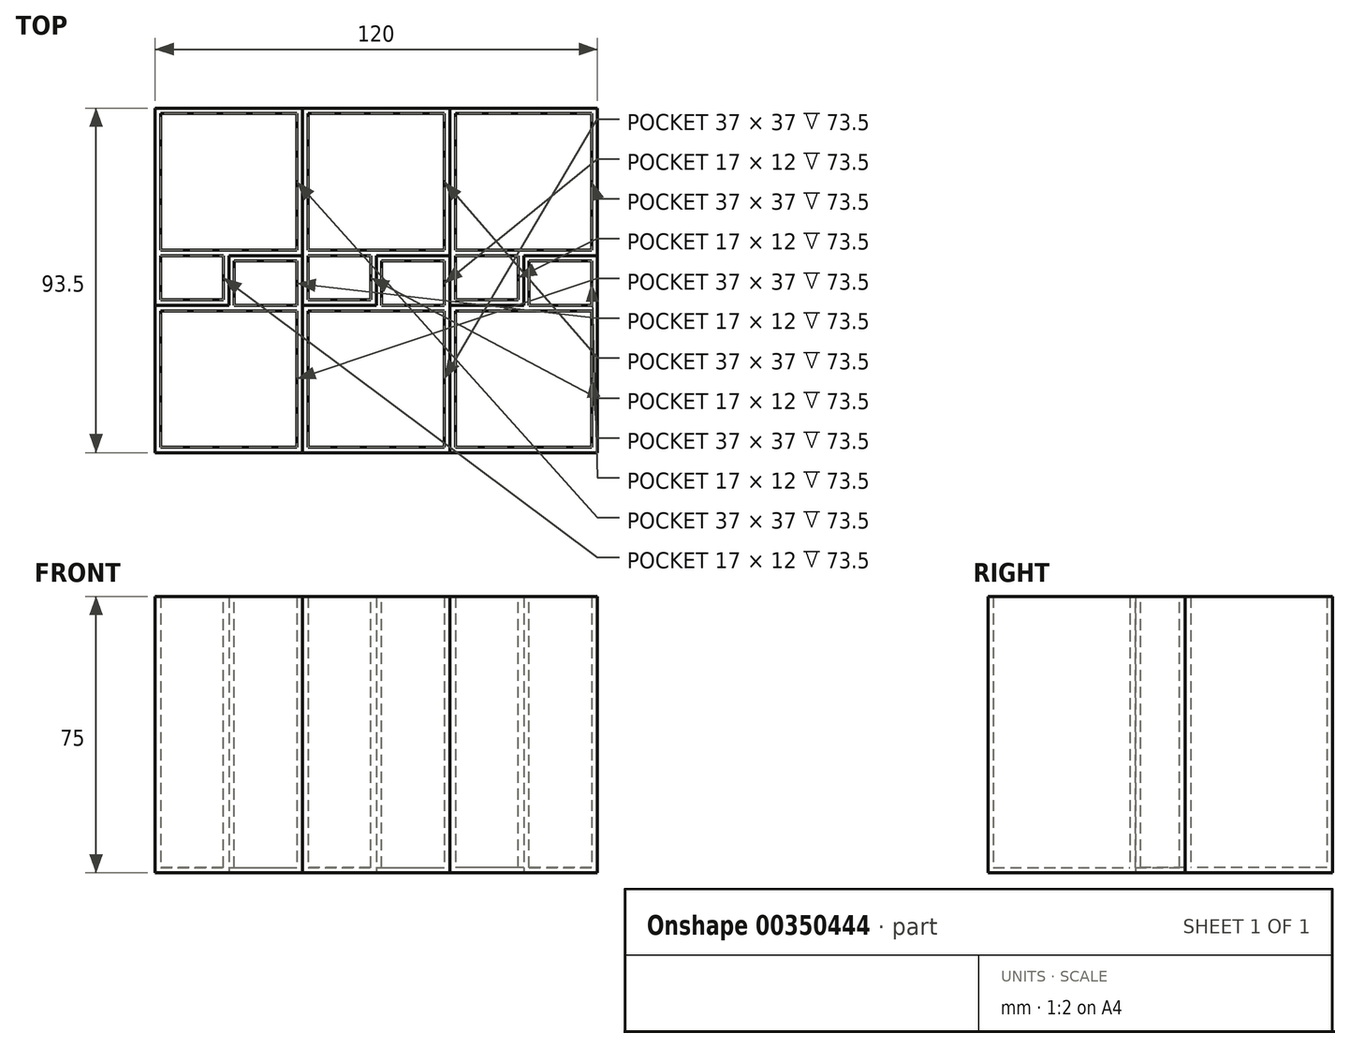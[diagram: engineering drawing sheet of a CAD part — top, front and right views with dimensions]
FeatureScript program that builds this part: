
annotation { "Feature Type Name" : "Feature", "Feature Type Description" : "" }
export const myFeature = defineFeature(function(context is Context, id is Id, definition is map)
    precondition{}
    {
        {
            var Q0;
            Q0=qCreatedBy(makeId("Top.planeOp"),FACE);
            var sketch = newSketch(context, id + "F0", { "sketchPlane" : qUnion([Q0])});
            skLineSegment(sketch, "E0.bottom", {"start": v(20, 20) * mm, "end": v(-20, 20) * mm});
            skLineSegment(sketch, "E0.top", {"start": v(20, -20) * mm, "end": v(-20, -20) * mm});
            skLineSegment(sketch, "E0.left", {"start": v(20, 20) * mm, "end": v(20, -20) * mm});
            skLineSegment(sketch, "E0.right", {"start": v(-20, 20) * mm, "end": v(-20, -20) * mm});
            skPoint(sketch, "E0.middle", {"position": v(0, 0) * mm});
            skSolve(sketch);
        }
        {
            var Q0;
            Q0 = qSketchRegion(id + "F0", true);
            extrude(context, id + "F1", {"entities" : qUnion([Q0]), "depth" : 75 * mm});
        }
        {
            var Q0;
            Q0=makeQuery(id+"F1.opExtrude","CAP_FACE",FACE,{"disambiguationData":[OSD([sQuery(id+"F0.wireOp",EDGE,"E0.bottom"),sQuery(id+"F0.wireOp",EDGE,"E0.top"),sQuery(id+"F0.wireOp",EDGE,"E0.left"),sQuery(id+"F0.wireOp",EDGE,"E0.right")])],"isStart":false});
            shell(context, id + "F2", {"entities" : qUnion([Q0]), "thickness" : 1.5 * mm});
        }
        {
            var Q0;
            Q0=qCreatedBy(makeId("Top.planeOp"),FACE);
            var sketch = newSketch(context, id + "F3", { "sketchPlane" : qUnion([Q0])});
            skLineSegment(sketch, "E1.bottom", {"start": v(-20, -20) * mm, "end": v(0, -20) * mm});
            skLineSegment(sketch, "E1.top", {"start": v(-20, -33.5) * mm, "end": v(0, -33.5) * mm});
            skLineSegment(sketch, "E1.left", {"start": v(-20, -20) * mm, "end": v(-20, -33.5) * mm});
            skLineSegment(sketch, "E1.right", {"start": v(0, -20) * mm, "end": v(0, -33.5) * mm});
            skSolve(sketch);
        }
        {
            var Q0;
            Q0 = qSketchRegion(id + "F3", true);
            var Q1;
            Q1=makeQuery(id+"F1.opExtrude","CAP_FACE",FACE,{"disambiguationData":[OSD([sQuery(id+"F0.wireOp",EDGE,"E0.bottom"),sQuery(id+"F0.wireOp",EDGE,"E0.top"),sQuery(id+"F0.wireOp",EDGE,"E0.left"),sQuery(id+"F0.wireOp",EDGE,"E0.right")])],"isStart":false});
            extrude(context, id + "F4", {"entities" : qUnion([Q0]), "operationType" : NewBodyOperationType.ADD, "endBound" : BoundingType.UP_TO_SURFACE, "endBoundEntityFace" : qUnion([Q1]), "depth" : 25 * mm});
        }
        {
            var Q0;
            Q0=makeQuery(id+"F4.boolean.opBoolean","MERGE",FACE,{"derivedFrom":[makeQuery(id+"F1.opExtrude","CAP_FACE",FACE,{"disambiguationData":[OSD([sQuery(id+"F0.wireOp",EDGE,"E0.bottom"),sQuery(id+"F0.wireOp",EDGE,"E0.top"),sQuery(id+"F0.wireOp",EDGE,"E0.left"),sQuery(id+"F0.wireOp",EDGE,"E0.right")])],"isStart":false}),makeQuery(id+"F4.opExtrude","CAP_FACE",FACE,{"disambiguationData":[OSD([sQuery(id+"F3.wireOp",EDGE,"E1.bottom"),sQuery(id+"F3.wireOp",EDGE,"E1.top"),sQuery(id+"F3.wireOp",EDGE,"E1.left"),sQuery(id+"F3.wireOp",EDGE,"E1.right")])],"isStart":false})]});
            var sketch = newSketch(context, id + "F5", { "sketchPlane" : qUnion([Q0])});
            skLineSegment(sketch, "E2.bottom", {"start": v(-18.5, -32) * mm, "end": v(-1.5, -32) * mm});
            skLineSegment(sketch, "E2.top", {"start": v(-18.5, -20) * mm, "end": v(-1.5, -20) * mm});
            skLineSegment(sketch, "E2.left", {"start": v(-18.5, -32) * mm, "end": v(-18.5, -20) * mm});
            skLineSegment(sketch, "E2.right", {"start": v(-1.5, -32) * mm, "end": v(-1.5, -20) * mm});
            skSolve(sketch);
        }
        {
            var Q0;
            Q0 = qSketchRegion(id + "F5", true);
            var Q1;
            Q1=makeQuery(id+"F2.opShell","OFFSET_FACE",FACE,{"disambiguationData":[OSD([sQuery(id+"F0.wireOp",EDGE,"E0.bottom"),sQuery(id+"F0.wireOp",EDGE,"E0.top"),sQuery(id+"F0.wireOp",EDGE,"E0.left"),sQuery(id+"F0.wireOp",EDGE,"E0.right")])]});
            extrude(context, id + "F6", {"entities" : qUnion([Q0]), "operationType" : NewBodyOperationType.REMOVE, "endBound" : BoundingType.UP_TO_SURFACE, "oppositeDirection" : true, "endBoundEntityFace" : qUnion([Q1]), "depth" : 25 * mm});
        }
        {
            var Q0;
            Q0=makeQuery(id+"F1.opExtrude","SWEPT_BODY",BODY,{"disambiguationData":[OSD([sQuery(id+"F0.wireOp",EDGE,"E0.bottom"),sQuery(id+"F0.wireOp",EDGE,"E0.top"),sQuery(id+"F0.wireOp",EDGE,"E0.left"),sQuery(id+"F0.wireOp",EDGE,"E0.right")])]});
            transform(context, id + "F7", {"entities" : qUnion([Q0]), "transformType" : TransformType.TRANSLATION_3D, "dx" : 40 * mm, "dy" : 0 * mm, "dz" : 0 * mm, "makeCopy" : true});
        }
        {
            var Q0;
            Q0=makeQuery(id+"F1.opExtrude","SWEPT_BODY",BODY,{"disambiguationData":[OSD([sQuery(id+"F0.wireOp",EDGE,"E0.bottom"),sQuery(id+"F0.wireOp",EDGE,"E0.top"),sQuery(id+"F0.wireOp",EDGE,"E0.left"),sQuery(id+"F0.wireOp",EDGE,"E0.right")])]});
            var Q1;
            Q1=makeQuery(id+"F1.opExtrude","SWEPT_EDGE",EDGE,{"disambiguationData":[OSD([sQuery(id+"F0.wireOp",EDGE,"E0.bottom"),sQuery(id+"F0.wireOp",EDGE,"E0.right")])]});
            transform(context, id + "F8", {"entities" : qUnion([Q0]), "transformType" : TransformType.ROTATION, "transformAxis" : qUnion([Q1]), "angle" : 180 * degree, "makeCopy" : true});
        }
        {
            var Q0;
            Q0=makeQuery(id+"F8.opPattern","COPY",BODY,{"derivedFrom":makeQuery(id+"F1.opExtrude","SWEPT_BODY",BODY,{"disambiguationData":[OSD([sQuery(id+"F0.wireOp",EDGE,"E0.bottom"),sQuery(id+"F0.wireOp",EDGE,"E0.top"),sQuery(id+"F0.wireOp",EDGE,"E0.left"),sQuery(id+"F0.wireOp",EDGE,"E0.right")])]}),"instanceName":"1"});
            var Q1;
            Q1=makeQuery(id+"F8.opPattern","COPY",VERTEX,{"derivedFrom":makeQuery(id+"F6.boolean.opBoolean","COPY",VERTEX,{"derivedFrom":makeQuery(id+"F6.opExtrude","CAP_VERTEX",VERTEX,{"disambiguationData":[OSD([sQuery(id+"F5.wireOp",EDGE,"E2.bottom"),sQuery(id+"F5.wireOp",EDGE,"E2.right")])],"isStart":true})}),"instanceName":"1"});
            var Q2;
            Q2=makeQuery(id+"F4.opExtrude","CAP_VERTEX",VERTEX,{"disambiguationData":[OSD([sQuery(id+"F3.wireOp",EDGE,"E1.bottom"),sQuery(id+"F3.wireOp",EDGE,"E1.right")])],"isStart":false});
            transform(context, id + "F9", {"entities" : qUnion([Q0]), "transformType" : TransformType.TRANSLATION_3D, "dx" : 40 * mm, "dy" : -93.5 * mm, "dz" : 0 * mm, "makeCopy" : false});
        }
        {
            var Q0;
            Q0=makeQuery(id+"F8.opPattern","COPY",BODY,{"derivedFrom":makeQuery(id+"F1.opExtrude","SWEPT_BODY",BODY,{"disambiguationData":[OSD([sQuery(id+"F0.wireOp",EDGE,"E0.bottom"),sQuery(id+"F0.wireOp",EDGE,"E0.top"),sQuery(id+"F0.wireOp",EDGE,"E0.left"),sQuery(id+"F0.wireOp",EDGE,"E0.right")])]}),"instanceName":"1"});
            transform(context, id + "F10", {"entities" : qUnion([Q0]), "transformType" : TransformType.TRANSLATION_3D, "dx" : 40 * mm, "dy" : 0 * mm, "dz" : 0 * mm, "makeCopy" : true});
        }
        {
            var Q0;
            Q0=makeQuery(id+"F1.opExtrude","SWEPT_BODY",BODY,{"disambiguationData":[OSD([sQuery(id+"F0.wireOp",EDGE,"E0.bottom"),sQuery(id+"F0.wireOp",EDGE,"E0.top"),sQuery(id+"F0.wireOp",EDGE,"E0.left"),sQuery(id+"F0.wireOp",EDGE,"E0.right")])]});
            transform(context, id + "F11", {"entities" : qUnion([Q0]), "transformType" : TransformType.TRANSLATION_3D, "dx" : 80 * mm, "dy" : 0 * mm, "dz" : 0 * mm, "makeCopy" : true});
        }
        {
            var Q0;
            Q0=makeQuery(id+"F8.opPattern","COPY",BODY,{"derivedFrom":makeQuery(id+"F1.opExtrude","SWEPT_BODY",BODY,{"disambiguationData":[OSD([sQuery(id+"F0.wireOp",EDGE,"E0.bottom"),sQuery(id+"F0.wireOp",EDGE,"E0.top"),sQuery(id+"F0.wireOp",EDGE,"E0.left"),sQuery(id+"F0.wireOp",EDGE,"E0.right")])]}),"instanceName":"1"});
            transform(context, id + "F12", {"entities" : qUnion([Q0]), "transformType" : TransformType.TRANSLATION_3D, "dx" : 80 * mm, "dy" : 0 * mm, "dz" : 0 * mm, "makeCopy" : true});
        }
    });
